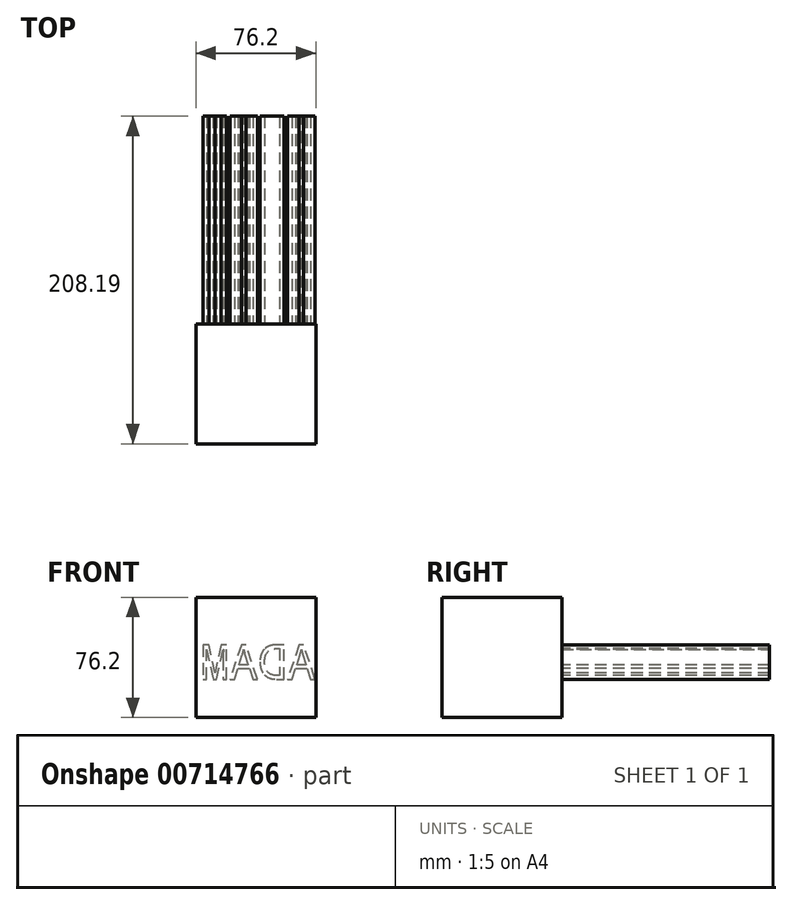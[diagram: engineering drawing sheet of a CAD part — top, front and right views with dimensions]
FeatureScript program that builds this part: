
annotation { "Feature Type Name" : "Feature", "Feature Type Description" : "" }
export const myFeature = defineFeature(function(context is Context, id is Id, definition is map)
    precondition{}
    {
        {
            var Q0;
            Q0=qCreatedBy(makeId("Front.planeOp"),FACE);
            var sketch = newSketch(context, id + "F0", { "sketchPlane" : qUnion([Q0])});
            skLineSegment(sketch, "E0.bottom", {"start": v(-44.36, 45.45) * mm, "end": v(31.84, 45.45) * mm});
            skLineSegment(sketch, "E0.top", {"start": v(-44.36, -30.75) * mm, "end": v(31.84, -30.75) * mm});
            skLineSegment(sketch, "E0.left", {"start": v(-44.36, 45.45) * mm, "end": v(-44.36, -30.75) * mm});
            skLineSegment(sketch, "E0.right", {"start": v(31.84, 45.45) * mm, "end": v(31.84, -30.75) * mm});
            skSolve(sketch);
        }
        {
            var Q0;
            Q0 = qSketchRegion(id + "F0", true);
            extrude(context, id + "F1", {"entities" : qUnion([Q0]), "depth" : 76.2 * mm, "offsetDistance" : 25.4 * mm});
        }
        {
            var Q0;
            Q0=makeQuery(id+"F1.opExtrude","CAP_FACE",FACE,{"disambiguationData":[OSD([sQuery(id+"F0.wireOp",EDGE,"E0.bottom"),sQuery(id+"F0.wireOp",EDGE,"E0.top"),sQuery(id+"F0.wireOp",EDGE,"E0.left"),sQuery(id+"F0.wireOp",EDGE,"E0.right")])],"isStart":true});
            var sketch = newSketch(context, id + "F2", { "sketchPlane" : qUnion([Q0])});
            skText(sketch, "E1", { "text": "ADAM", "fontName": "DroidSansMono.ttf"});
            const initialGuessF2  = {"E1": [-0.03183, -0.00652, 1, 0, 0.02199]};
            skSetInitialGuess(sketch, initialGuessF2);
            skSolve(sketch);
        }
        {
            var Q0;
            Q0 = qSketchRegion(id + "F2", true);
            extrude(context, id + "F3", {"entities" : qUnion([Q0]), "operationType" : NewBodyOperationType.ADD, "endBound" : BoundingType.THROUGH_ALL, "depth" : 101.6 * mm, "offsetDistance" : 25.4 * mm});
        }
    });
